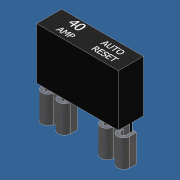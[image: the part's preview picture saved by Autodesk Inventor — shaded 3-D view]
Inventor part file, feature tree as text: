
AUTODESK INVENTOR PART (.ipt)
format: ipt  version: 2012 (Build 160160000, 160)  size: 363,520 bytes
history: native  units: mm (DEFAULTED — no unit token found)
features: extrude x4, sketch x4, plane x3, mirror x1, projected_geometry x1
ambient origin geometry x5: Origin, X Axis, Y Axis, Z Axis, Center Point
bodies: Solid1 (feature_tree)
feature tree (13):
  extrude  "Extrusion1"  Depth=8.89mm
  extrude  "Extrusion2"  Depth=0.8128mm
  extrude  "Extrusion3"  Depth=12.446mm TaperAngle=0.0deg
  mirror  "Mirror1"
  extrude  "Extrusion4"  Depth=10.16mm
  plane  "YZ Plane (RIGHT)"
  plane  "XZ Plane (TOP)"
  plane  "XY Plane (FRONT)"
  sketch  "Sketch2"  dims[d0=28.956mm d1=8.89mm]
  sketch  "Sketch3"  dims[d2=18.288mm d3=0.0mm d4=0.8128mm]
  sketch  "Sketch4"  dims[d5=8.001mm d6=12.446mm d7=0.0mm]
  projected_geometry  "Projected Loop1"
  sketch  "Sketch5"  dims[d8=0.5588mm d9=10.16mm d10=4.6482mm d11=1.524mm d12=9.652mm d13=0.0mm d14=0.00254mm d15=0.0mm]
